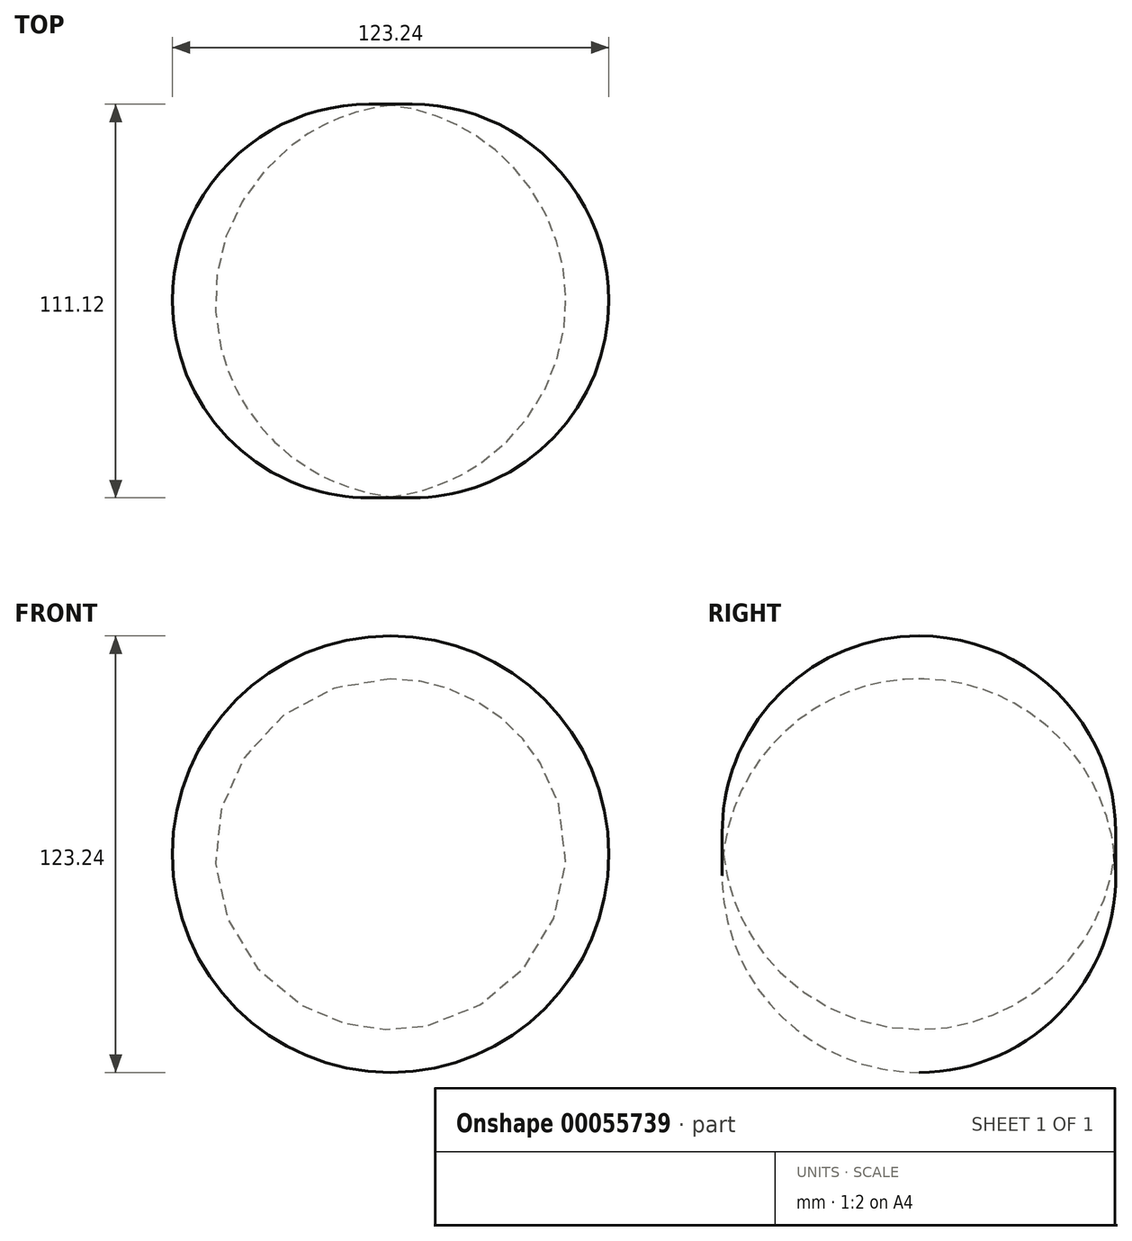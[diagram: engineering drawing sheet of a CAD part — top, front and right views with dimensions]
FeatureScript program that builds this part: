
annotation { "Feature Type Name" : "Feature", "Feature Type Description" : "" }
export const myFeature = defineFeature(function(context is Context, id is Id, definition is map)
    precondition{}
    {
        {
            var Q0;
            Q0=qCreatedBy(makeId("Right.planeOp"),FACE);
            var sketch = newSketch(context, id + "F0", { "sketchPlane" : qUnion([Q0])});
            skLineSegment(sketch, "E0", {"start": v(-54.4, 0) * mm, "end": v(56.07, 0) * mm});
            skArc(sketch, "E1", {"start": v(-54.4, 0) * mm, "mid": v(0.84, -49.5) * mm, "end": v(56.07, 0) * mm});
            skSolve(sketch);
        }
        {
            var Q0;
            Q0 = qSketchRegion(id + "F0", true);
            var Q1;
            Q1=sQuery(id+"F0.wireOp",EDGE,"E0");
            revolve(context, id + "F1", {"entities" : qUnion([Q0]), "axis" : qUnion([Q1]), "revolveType" : RevolveType.FULL});
        }
    });
